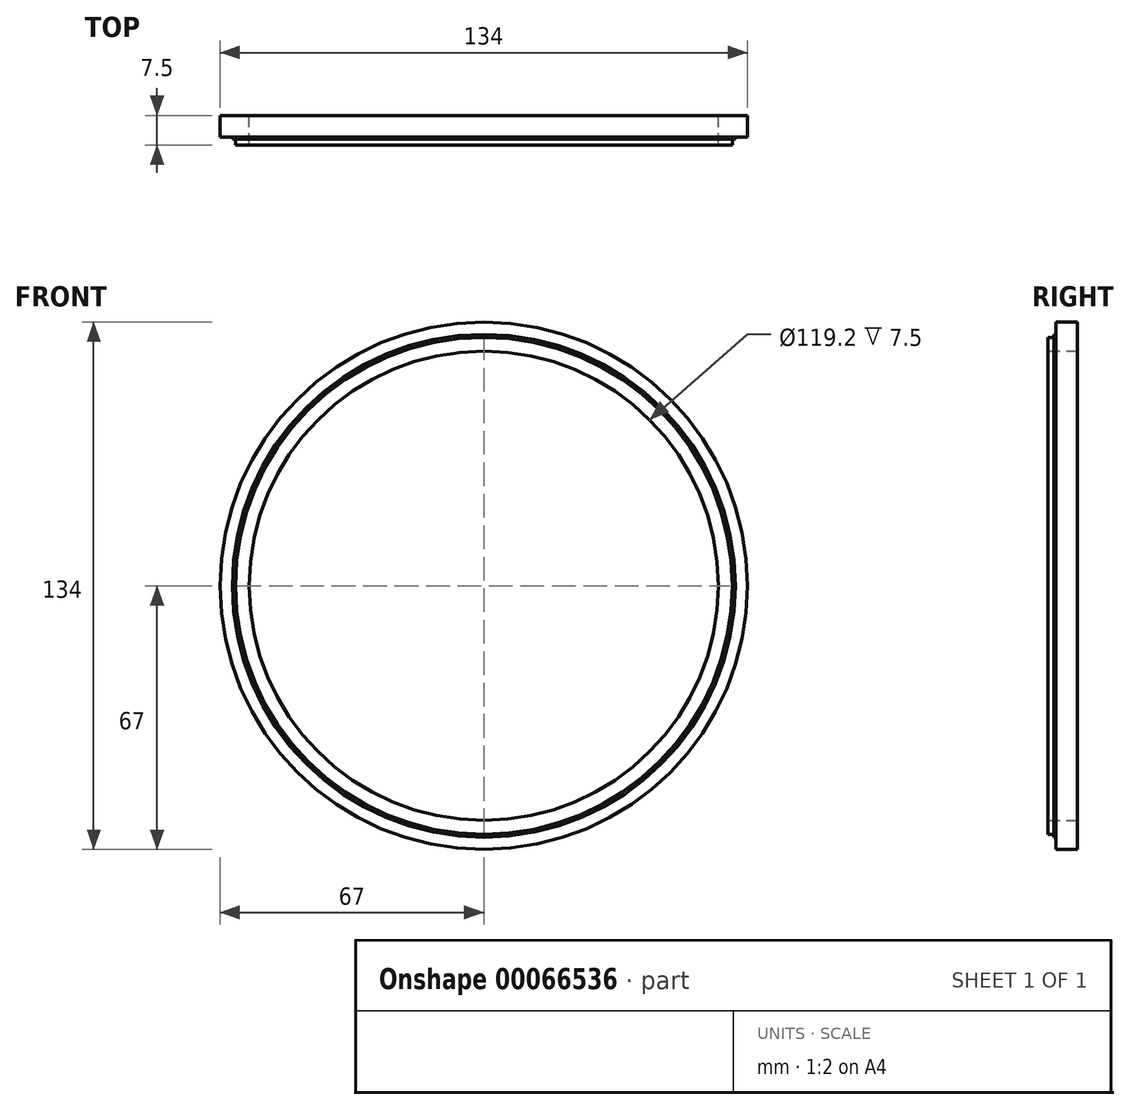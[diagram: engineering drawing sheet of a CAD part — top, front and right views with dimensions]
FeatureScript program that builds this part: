
annotation { "Feature Type Name" : "Feature", "Feature Type Description" : "" }
export const myFeature = defineFeature(function(context is Context, id is Id, definition is map)
    precondition{}
    {
        {
            var Q0;
            Q0=qCreatedBy(makeId("Front.planeOp"),FACE);
            var sketch = newSketch(context, id + "F0", { "sketchPlane" : qUnion([Q0])});
            skCircle(sketch, "E0", {"center": v(0, 0) * mm, "radius": 59.6 * mm});
            skCircle(sketch, "E1", {"center": v(0, 0) * mm, "radius": 67 * mm});
            skSolve(sketch);
        }
        {
            var Q0;
            Q0=makeQuery(id+"F0.imprint","IMPRINT",FACE,{"disambiguationData":[TD([[makeQuery(id+"F0.imprint","IMPRINT",EDGE,{"derivedFrom":sQuery(id+"F0.wireOp",EDGE,"E0")}),-1.0]])]});
            extrude(context, id + "F1", {"entities" : qUnion([Q0]), "endBound" : BoundingType.SYMMETRIC, "depth" : 7.5 * mm});
        }
        {
            var Q0;
            Q0=makeQuery(id+"F1.opExtrude","CAP_FACE",FACE,{"disambiguationData":[OSD([sQuery(id+"F0.wireOp",EDGE,"E0"),sQuery(id+"F0.wireOp",EDGE,"E1")])],"isStart":false});
            var sketch = newSketch(context, id + "F2", { "sketchPlane" : qUnion([Q0])});
            skCircle(sketch, "E2", {"center": v(0, 0) * mm, "radius": 63.88 * mm});
            skCircle(sketch, "E3", {"center": v(0, 0) * mm, "radius": 63.12 * mm});
            skSolve(sketch);
        }
        {
            var Q0;
            Q0=makeQuery(id+"F2.imprint","IMPRINT",FACE,{"disambiguationData":[TD([[makeQuery(id+"F2.imprint","IMPRINT",EDGE,{"derivedFrom":sQuery(id+"F2.wireOp",EDGE,"E2")}),1.0]])]});
            extrude(context, id + "F3", {"entities" : qUnion([Q0]), "operationType" : NewBodyOperationType.REMOVE, "oppositeDirection" : true, "depth" : 1.5 * mm});
        }
        {
            var Q0;
            {var subQ0=sQuery(id+"F0.wireOp",EDGE,"E1");Q0=makeQuery(id+"F3.boolean.opBoolean","SPLIT",FACE,{"disambiguationData":[TD([makeQuery(id+"F1.opExtrude","SWEPT_FACE",FACE,{"disambiguationData":[OSD([subQ0])]})])],"derivedFrom":makeQuery(id+"F1.opExtrude","CAP_FACE",FACE,{"disambiguationData":[OSD([sQuery(id+"F0.wireOp",EDGE,"E0"),subQ0])],"isStart":false})});}
            extrude(context, id + "F4", {"entities" : qUnion([Q0]), "operationType" : NewBodyOperationType.REMOVE, "oppositeDirection" : true, "depth" : 2 * mm});
        }
    });
